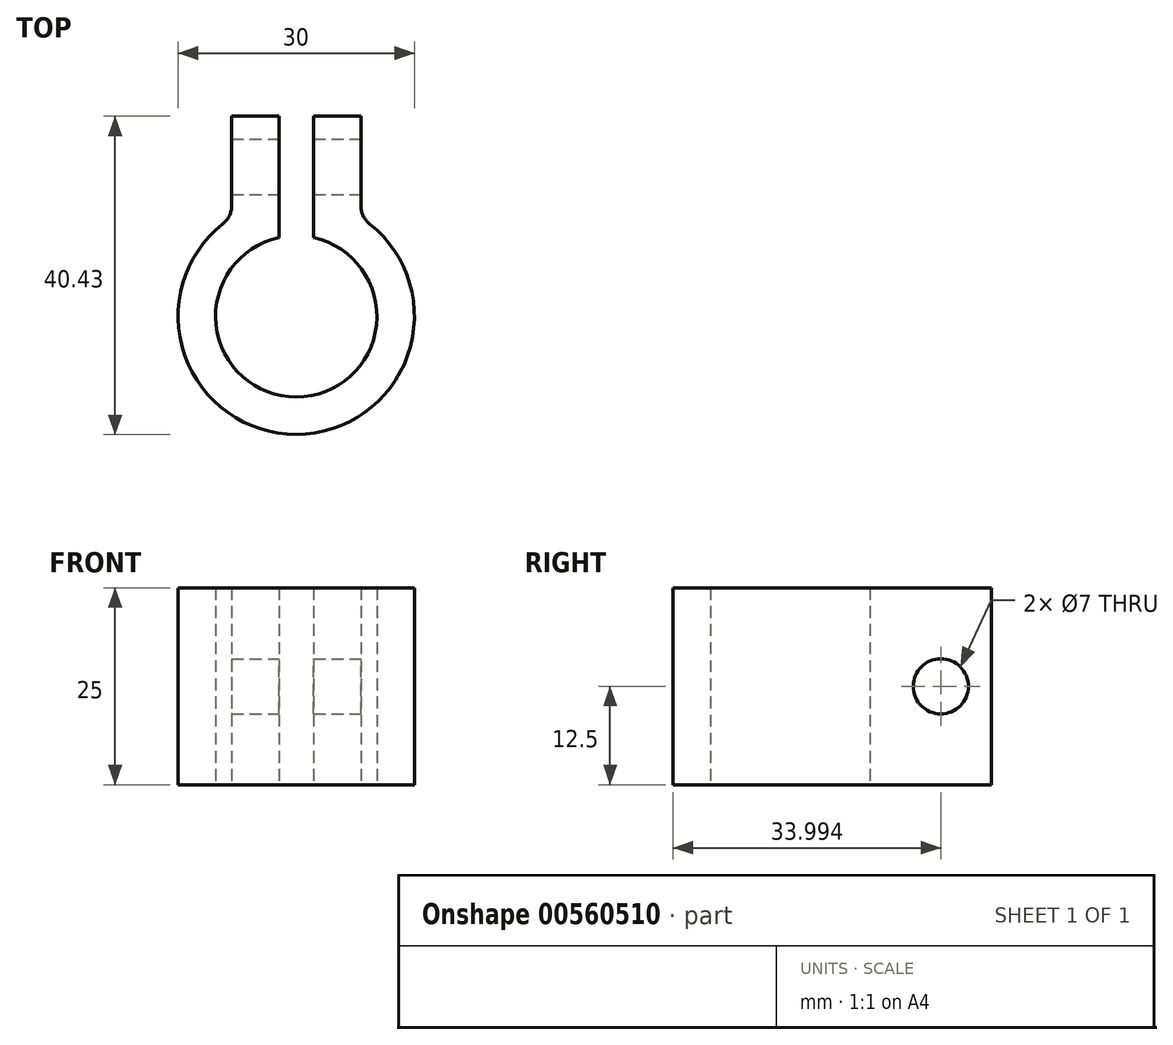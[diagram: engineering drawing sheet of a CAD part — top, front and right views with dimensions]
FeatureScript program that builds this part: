
annotation { "Feature Type Name" : "Feature", "Feature Type Description" : "" }
export const myFeature = defineFeature(function(context is Context, id is Id, definition is map)
    precondition{}
    {
        {
            var Q0;
            Q0=qCreatedBy(makeId("Top.planeOp"),FACE);
            var sketch = newSketch(context, id + "F0", { "sketchPlane" : qUnion([Q0])});
            skCircle(sketch, "E0", {"center": v(0, 0) * mm, "radius": 15 * mm});
            skCircle(sketch, "E1", {"center": v(0, 0) * mm, "radius": 10.25 * mm});
            skLineSegment(sketch, "E2", {"start": v(-8.2, 12.56) * mm, "end": v(-8.2, 25.43) * mm});
            skLineSegment(sketch, "E3", {"start": v(-8.2, 25.43) * mm, "end": v(-2.2, 25.43) * mm});
            skLineSegment(sketch, "E4", {"start": v(-2.2, 25.43) * mm, "end": v(-2.2, 14.84) * mm});
            skLineSegment(sketch, "E5", {"start": v(2.2, 14.84) * mm, "end": v(2.2, 25.43) * mm});
            skLineSegment(sketch, "E6", {"start": v(2.2, 25.43) * mm, "end": v(8.2, 25.43) * mm});
            skLineSegment(sketch, "E7", {"start": v(8.2, 25.43) * mm, "end": v(8.2, 12.56) * mm});
            skLineSegment(sketch, "E8", {"start": v(2.2, 14.84) * mm, "end": v(2.2, 10) * mm});
            skLineSegment(sketch, "E9", {"start": v(-2.2, 14.84) * mm, "end": v(-2.2, 10) * mm});
            skSolve(sketch);
        }
        {
            var Q0;
            Q0=makeQuery(id+"F0.imprint","IMPRINT",FACE,{"disambiguationData":[TD([[makeQuery(id+"F0.imprint","IMPRINT",EDGE,{"derivedFrom":sQuery(id+"F0.wireOp",EDGE,"E0")}),1.0]])]});
            var Q1;
            {var subQ0=sQuery(id+"F0.wireOp",EDGE,"E2");Q1=makeQuery(id+"F0.imprint","IMPRINT",FACE,{"disambiguationData":[TD([[makeQuery(id+"F0.imprint","IMPRINT",EDGE,{"derivedFrom":subQ0}),-1.0]])]});}
            var Q2;
            {var subQ0=sQuery(id+"F0.wireOp",EDGE,"E5");Q2=makeQuery(id+"F0.imprint","IMPRINT",FACE,{"disambiguationData":[TD([[makeQuery(id+"F0.imprint","IMPRINT",EDGE,{"derivedFrom":subQ0}),-1.0]])]});}
            extrude(context, id + "F1", {"entities" : qUnion([Q0, Q1, Q2]), "depth" : 25 * mm, "offsetDistance" : 25 * mm});
        }
        {
            var Q0;
            Q0=makeQuery(id+"F1.opExtrude","SWEPT_FACE",FACE,{"disambiguationData":[OSD([sQuery(id+"F0.wireOp",EDGE,"E7")])]});
            var sketch = newSketch(context, id + "F2", { "sketchPlane" : qUnion([Q0])});
            skCircle(sketch, "E10", {"center": v(19, 12.5) * mm, "radius": 3.5 * mm});
            skSolve(sketch);
        }
        {
            var Q0;
            Q0=makeQuery(id+"F2.imprint","IMPRINT",FACE,{"disambiguationData":[TD([[makeQuery(id+"F2.imprint","IMPRINT",EDGE,{"derivedFrom":sQuery(id+"F2.wireOp",EDGE,"E10")}),1.0]])]});
            extrude(context, id + "F3", {"entities" : qUnion([Q0]), "operationType" : NewBodyOperationType.REMOVE, "oppositeDirection" : true, "depth" : 25 * mm, "offsetDistance" : 25 * mm});
        }
        {
            var Q0;
            Q0=makeQuery(id+"F1.opExtrude","SWEPT_EDGE",EDGE,{"disambiguationData":[OSD([sQuery(id+"F0.wireOp",EDGE,"E0"),sQuery(id+"F0.wireOp",EDGE,"E7")])]});
            var Q1;
            Q1=makeQuery(id+"F1.opExtrude","SWEPT_EDGE",EDGE,{"disambiguationData":[OSD([sQuery(id+"F0.wireOp",EDGE,"E0"),sQuery(id+"F0.wireOp",EDGE,"E2")])]});
            fillet(context, id + "F4", {"entities" : qUnion([Q0, Q1]), "radius" : 3 * mm, "tangentPropagation" : true, "allowEdgeOverflow" : false});
        }
    });
